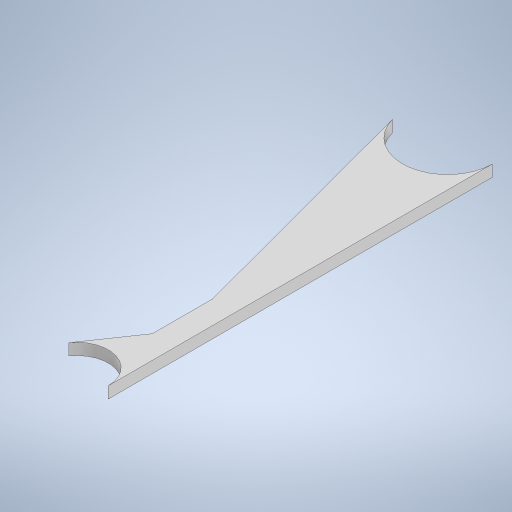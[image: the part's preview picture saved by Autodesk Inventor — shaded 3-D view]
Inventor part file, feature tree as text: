
AUTODESK INVENTOR PART (.ipt)
format: ipt  version: 2024 (Build 280153000, 153)  size: 251,392 bytes
history: native  units: mm
features: extrude x1, sketch x1
ambient origin geometry x8: Origin, YZ Plane, XZ Plane, XY Plane, X Axis, Y Axis, Z Axis, Center Point
bodies: Solid1 (feature_tree)
feature tree (2):
  extrude  "Extrusion1"  Depth=20.0mm
  sketch  "Sketch1"  dims[d0=600.0mm d1=200.0mm d2=160.0mm d3=20.0mm d4=20.0mm d5=20.0mm d6=0.0mm]
